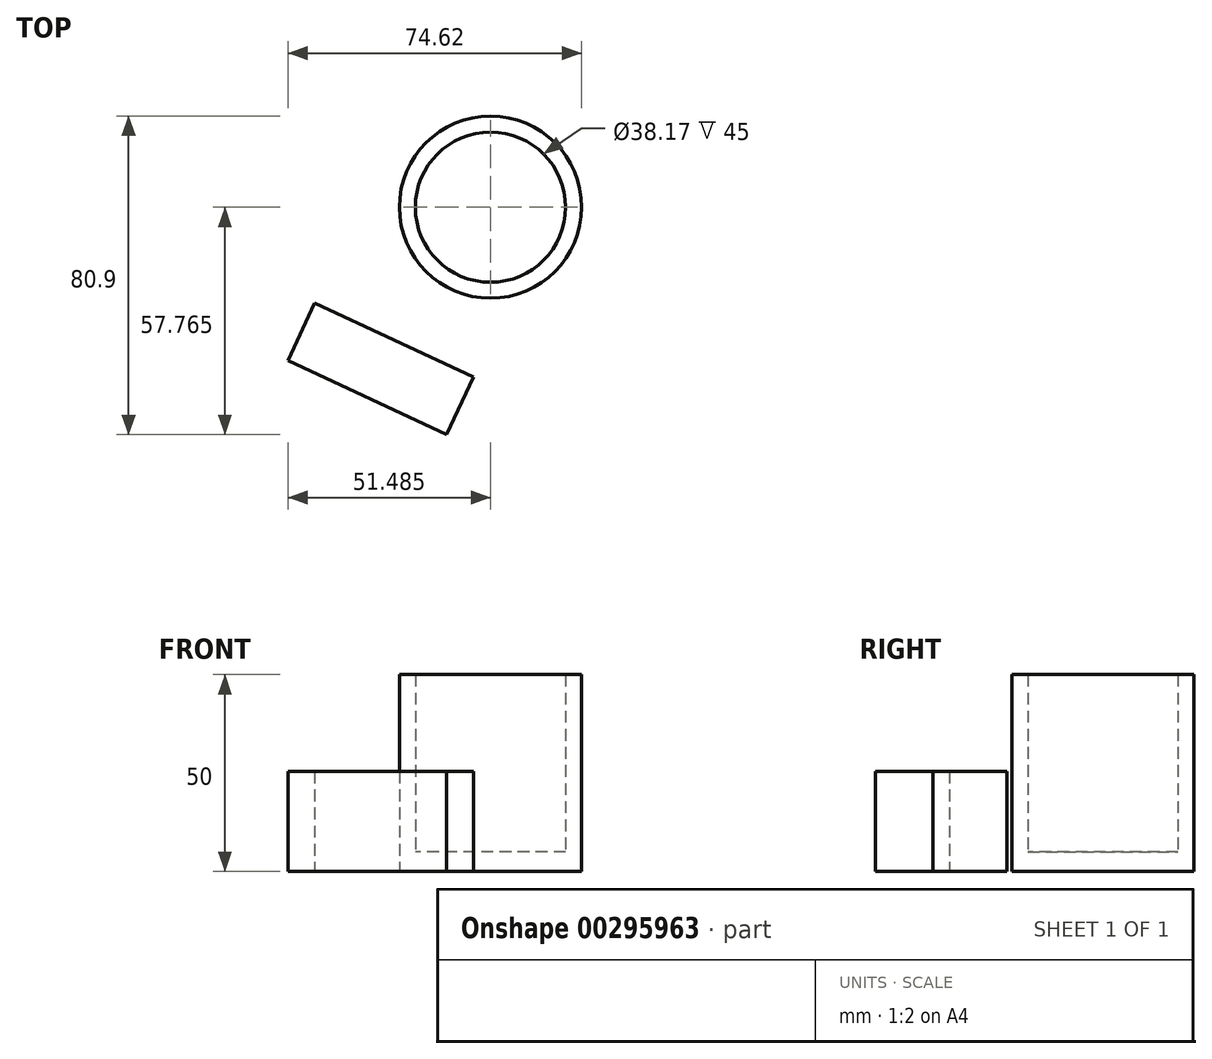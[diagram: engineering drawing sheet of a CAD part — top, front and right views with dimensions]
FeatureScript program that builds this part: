
annotation { "Feature Type Name" : "Feature", "Feature Type Description" : "" }
export const myFeature = defineFeature(function(context is Context, id is Id, definition is map)
    precondition{}
    {
        {
            var Q0;
            Q0=qCreatedBy(makeId("Top.planeOp"),FACE);
            var sketch = newSketch(context, id + "F0", { "sketchPlane" : qUnion([Q0])});
            skCircle(sketch, "E0", {"center": v(-53.28, 39.06) * mm, "radius": 23.14 * mm});
            skCircle(sketch, "E1", {"center": v(-53.28, 39.06) * mm, "radius": 19.09 * mm});
            skSolve(sketch);
        }
        {
            var Q0;
            Q0=makeQuery(id+"F0.imprint","IMPRINT",FACE,{"disambiguationData":[TD([[makeQuery(id+"F0.imprint","IMPRINT",EDGE,{"derivedFrom":sQuery(id+"F0.wireOp",EDGE,"E0")}),1.0]])]});
            extrude(context, id + "F1", {"entities" : qUnion([Q0]), "depth" : 50 * mm});
        }
        {
            var Q0;
            Q0=makeQuery(id+"F0.imprint","IMPRINT",FACE,{"disambiguationData":[TD([[makeQuery(id+"F0.imprint","IMPRINT",EDGE,{"derivedFrom":sQuery(id+"F0.wireOp",EDGE,"E1")}),1.0]])]});
            extrude(context, id + "F2", {"entities" : qUnion([Q0]), "operationType" : NewBodyOperationType.ADD, "depth" : 5 * mm});
        }
        {
            var Q0;
            Q0=makeQuery(id+"F1.opExtrude","SWEPT_BODY",BODY,{"disambiguationData":[OSD([sQuery(id+"F0.wireOp",EDGE,"E0"),sQuery(id+"F0.wireOp",EDGE,"E1")])]});
            transform(context, id + "F3", {"entities" : qUnion([Q0]), "transformType" : TransformType.TRANSLATION_3D, "dx" : 19.8 * mm, "dy" : -32.5 * mm, "dz" : 0 * mm, "makeCopy" : false});
        }
        {
            var Q0;
            Q0=qCreatedBy(makeId("Top.planeOp"),FACE);
            var sketch = newSketch(context, id + "F4", { "sketchPlane" : qUnion([Q0])});
            skLineSegment(sketch, "E2.bottom", {"start": v(-47.77, 63.6) * mm, "end": v(-3.27, 63.6) * mm});
            skLineSegment(sketch, "E2.top", {"start": v(-47.77, 47.5) * mm, "end": v(-3.27, 47.5) * mm});
            skLineSegment(sketch, "E2.left", {"start": v(-47.77, 63.6) * mm, "end": v(-47.77, 47.5) * mm});
            skLineSegment(sketch, "E2.right", {"start": v(-3.27, 63.6) * mm, "end": v(-3.27, 47.5) * mm});
            skSolve(sketch);
        }
        {
            var Q0;
            Q0 = qSketchRegion(id + "F4", true);
            extrude(context, id + "F5", {"entities" : qUnion([Q0]), "depth" : 25.4 * mm});
        }
        {
            var Q0;
            Q0=makeQuery(id+"F5.opExtrude","SWEPT_BODY",BODY,{"disambiguationData":[OSD([sQuery(id+"F4.wireOp",EDGE,"E2.bottom"),sQuery(id+"F4.wireOp",EDGE,"E2.top"),sQuery(id+"F4.wireOp",EDGE,"E2.left"),sQuery(id+"F4.wireOp",EDGE,"E2.right")])]});
            var Q1;
            Q1=makeQuery(id+"F1.opExtrude","CAP_EDGE",EDGE,{"disambiguationData":[OSD([sQuery(id+"F0.wireOp",EDGE,"E0")])],"isStart":false});
            transform(context, id + "F6", {"entities" : qUnion([Q0]), "transformType" : TransformType.ROTATION, "transformAxis" : qUnion([Q1]), "angle" : 155 * degree, "makeCopy" : false});
        }
    });
